# Revit family: 56_WTH_C2050 verdeler_e
name_source: partatom
category: Mechanical Equipment
revit_build: Autodesk Revit MEP 2012 (Build: 20110916_2132(x64)
units: mm (PartAtom-declared; Revit-internal decimal feet)

## types (28) — shared parameters
Description = C2050 Kunststof verdeler
Manufacturer = WTH Vloerverwarming B.V.
URL = http://www.wth.nl
content_modified_date = 08-08-2013
content_version = 1.0
datasheet = http://www.wth.nl
leverancier = WTH Vloerverwarming B.V.
lod_niveau = LOD 400
x = 55 mm  [stored 0.180446 ft]

## per-type parameters (varying)
| type | Model | aantal | afstand_x_cva | afstand_x_cvr | artikelnummer | bestelnummer | type verdeler |
| C2050 14 groepen rechts | 14 groepen rechts | 14 | 902 mm | 902 mm | B934 | B934 | 56_WTH_C2050 verdeler_geometrie : C2050 14 groepen rechts |
| C2050 14 groepen links | 14 groepen links | 14 | -132 mm | -132 mm | B934 | B934 | 56_WTH_C2050 verdeler_geometrie : C2050 14 groepen links |
| C2050 15 groepen links | 15 groepen links | 15 | -132 mm | -132 mm | B935 | B935 | 56_WTH_C2050 verdeler_geometrie : C2050 15 groepen links |
| C2050 15 groepen rechts | 15 groepen rechts | 15 | 957 mm | 957 mm | B935 | B935 | 56_WTH_C2050 verdeler_geometrie : C2050 15 groepen rechts |
| C2050 13 groepen links | 13 groepen links | 13 | -132 mm | -132 mm | B933 | B933 | 56_WTH_C2050 verdeler_geometrie : C2050 13 groepen links |
| C2050 13 groepen rechts | 13 groepen rechts | 13 | 847 mm | 847 mm | B933 | B933 | 56_WTH_C2050 verdeler_geometrie : C2050 13 groepen rechts |
| C2050 12 groepen links | 12 groepen links | 12 | -132 mm | -132 mm | B932 | B932 | 56_WTH_C2050 verdeler_geometrie : C2050 12 groepen links |
| C2050 12 groepen rechts | 12 groepen rechts | 12 | 792 mm | 792 mm | B932 | B932 | 56_WTH_C2050 verdeler_geometrie : C2050 12 groepen rechts |
| C2050 11 groepen links | 11 groepen links | 11 | -132 mm | -132 mm | B931 | B931 | 56_WTH_C2050 verdeler_geometrie : C2050 11 groepen links |
| C2050 11 groepen rechts | 11 groepen rechts | 11 | 737 mm | 737 mm | B931 | B931 | 56_WTH_C2050 verdeler_geometrie : C2050 11 groepen rechts |
| C2050 10 groepen links | 10 groepen links | 10 | -132 mm | -132 mm | B930 | B930 | 56_WTH_C2050 verdeler_geometrie : C2050 10 groepen links |
| C2050 9 groepen links | 9 groepen links | 9 | -132 mm | -132 mm | B929 | B929 | 56_WTH_C2050 verdeler_geometrie : C2050 9 groepen links |
| C2050 8 groepen links | 8 groepen links | 8 | -132 mm | -132 mm | B928 | B928 | 56_WTH_C2050 verdeler_geometrie : C2050 8 groepen links |
| C2050 7 groepen links | 7 groepen links | 7 | -132 mm | -132 mm | B927 | B927 | 56_WTH_C2050 verdeler_geometrie : C2050 7 groepen links |
| C2050 6 groepen links | 6 groepen links | 6 | -132 mm | -132 mm | B926 | B926 | 56_WTH_C2050 verdeler_geometrie : C2050 6 groepen links |
| C2050 5 groepen links | 5 groepen links | 5 | -132 mm | -132 mm | B925 | B925 | 56_WTH_C2050 verdeler_geometrie : C2050 5 groepen links |
| C2050 4 groepen links | 4 groepen links | 4 | -132 mm | -132 mm | B924 | B924 | 56_WTH_C2050 verdeler_geometrie : C2050 4 groepen links |
| C2050 3 groepen links | 3 groepen links | 3 | -132 mm | -132 mm | B923 | B923 | 56_WTH_C2050 verdeler_geometrie : C2050 3 groepen links |
| C2050 2 groepen links | 2 groepen links | 2 | -132 mm | -132 mm | B922 | B922 | 56_WTH_C2050 verdeler_geometrie : C2050 2 groepen links |
| C2050 10 groepen rechts | 10 groepen rechts | 10 | 682 mm | 682 mm | B930 | B930 | 56_WTH_C2050 verdeler_geometrie : C2050 10 groepen rechts |
| C2050 9 groepen rechts | 9 groepen rechts | 9 | 627 mm | 627 mm | B929 | B929 | 56_WTH_C2050 verdeler_geometrie : C2050 9 groepen rechts |
| C2050 8 groepen rechts | 8 groepen rechts | 8 | 572 mm | 572 mm | B928 | B928 | 56_WTH_C2050 verdeler_geometrie : C2050 8 groepen rechts |
| C2050 7 groepen rechts | 7 groepen rechts | 7 | 517 mm | 517 mm | B927 | B927 | 56_WTH_C2050 verdeler_geometrie : C2050 7 groepen rechts |
| C2050 6 groepen rechts | 6 groepen rechts | 6 | 462 mm | 462 mm | B926 | B926 | 56_WTH_C2050 verdeler_geometrie : C2050 6 groepen rechts |
| C2050 5 groepen rechts | 5 groepen rechts | 5 | 407 mm | 407 mm | B925 | B925 | 56_WTH_C2050 verdeler_geometrie : C2050 5 groepen rechts |
| C2050 4 groepen rechts | 4 groepen rechts | 4 | 352 mm | 352 mm | B924 | B924 | 56_WTH_C2050 verdeler_geometrie : C2050 4 groepen rechts |
| C2050 3 groepen rechts | 3 groepen rechts | 3 | 297 mm | 297 mm | B923 | B923 | 56_WTH_C2050 verdeler_geometrie : C2050 3 groepen rechts |
| C2050 2 groepen rechts | 2 groepen rechts | 2 | 242 mm | 242 mm | B922 | B922 | 56_WTH_C2050 verdeler_geometrie : C2050 2 groepen rechts |

note: [stored X ft] marks values corroborated as IEEE doubles in the binary element streams (Revit-internal decimal feet)

## geometry (parser evidence)
native form markers: Sweep x25
no freeform markers — native parametric forms only
